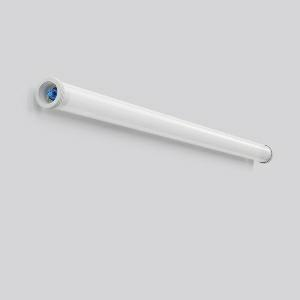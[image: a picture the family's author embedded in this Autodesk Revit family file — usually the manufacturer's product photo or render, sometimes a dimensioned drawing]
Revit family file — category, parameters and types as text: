
# Revit family: planox_tube_601072_002_1_4d05
name_source: partatom
category: Lighting Fixtures
units: mm (PartAtom-declared; Revit-internal decimal feet)

## family parameters
Cut with Voids When Loaded = No
Host = Face
Light Source = No
Part Type = Normal
Room Calculation Point = No
Round Connector Dimension = Use Diameter
Shared = No

## types (1)
- PLANOX TUBE (1 x LED Modul 840, 8650 lm, 4000)
    Apparent Load = 62 VA
    CIE Flux Codes = 42 71 90 91 100
    Color Rendering = 80
    Color Temperature = 4000
    Default Elevation = 1800 mm
    Description = Series: PLANOX TUBE
Robust protective tube luminaire for tough requirements. Rack made of sheet steel, white powder coated. End caps made of plastic (polyamide) grey. Diffuser made of plastic (polycarbonate), opal, shockproof. Symmetrical light distribution. Homogeneous light distribution. With accessories for wall, ceiling or pendant mounting. Driver integrated. Easy installation with the Plug+Play Wieland RST CLASSIC plug-in system. Luminaire with integrated through-wiring for series connection of further luminaires by two Wieland RST Classic plug connectors (plug and socket). Accessories for electrical connection must be ordered separately. Mounting set must be ordered separately. Luminaire with limited surface temperature in accordance with EN 60598-2-24 for use in environments in which a deposit of conductive dust on the luminaire can be expected. Qualified for use in the food and drink industry. Suitable for lighting in public car parks and public off-street parking spaces according to DIN 67528. Environmentally friendly and resource-saving due to replaceable components. 
Colour: white
Diameter: 78 mm
Length: 1564 mm
Lamp: LED
Socket: without socket
Colour temperature: 4000K
Colour rendering index (CRI): 83
System power: 62 W
Rated luminous flux: 8650 lm
Luminous efficiency: 140 lm/W
Control gear: Regulated power supply
Protection class: I
Type of protection: IP 67
    Height = 0 mm  [stored 0 ft]
    Lamp = 1 x LED Modul 840
    Lamp Light Flux = 8650 lm
    Lamp count = 1
    Length = 1564 mm
    Lifetime = 50000 h
    Luminous efficacy = 140 lm/W
    Manufacturer = RZB
    ModVariant = No
    Model = 601072.002.1
    Mounting Place = Ceiling
    Mounting Type = Surface mounted
    Number of Poles = 1
    OnlyDefault = Yes
    Power Factor = 1
    Product Name = PLANOX TUBE
    Product group = Surface mounted luminaires for moist/humid enviroments
    ProductGroupID = 308
    Protection Class = Protection class I
    Protection Degree = Degree of protection
    RLX_Detail_Level = 1
    RLX_Emergency_Light_Flux = 0 lm
    RLX_Emergency_Type = 0
    RLX_Emergency_Type_DB = No
    RlxData = <blob elided: 35197 chars, md5=ae118e64>
    Socket = socket
    Standby Power = 0 W
    System Light Flux = 8650 lm
    System Power = 62 W
    Type Comments = Product without accessories
    Type Image = 601072.002.jpg
    URL = http://relux.com
    VarID = ---
    Voltage = 0 V
    Weight = 0.00 kg
    Width = 0 mm  [stored 0 ft]

note: [stored X ft] marks values corroborated as IEEE doubles in the binary element streams (Revit-internal decimal feet)

## geometry (parser evidence)
native form markers: Blend x4, Sweep x14
no freeform markers — native parametric forms only
